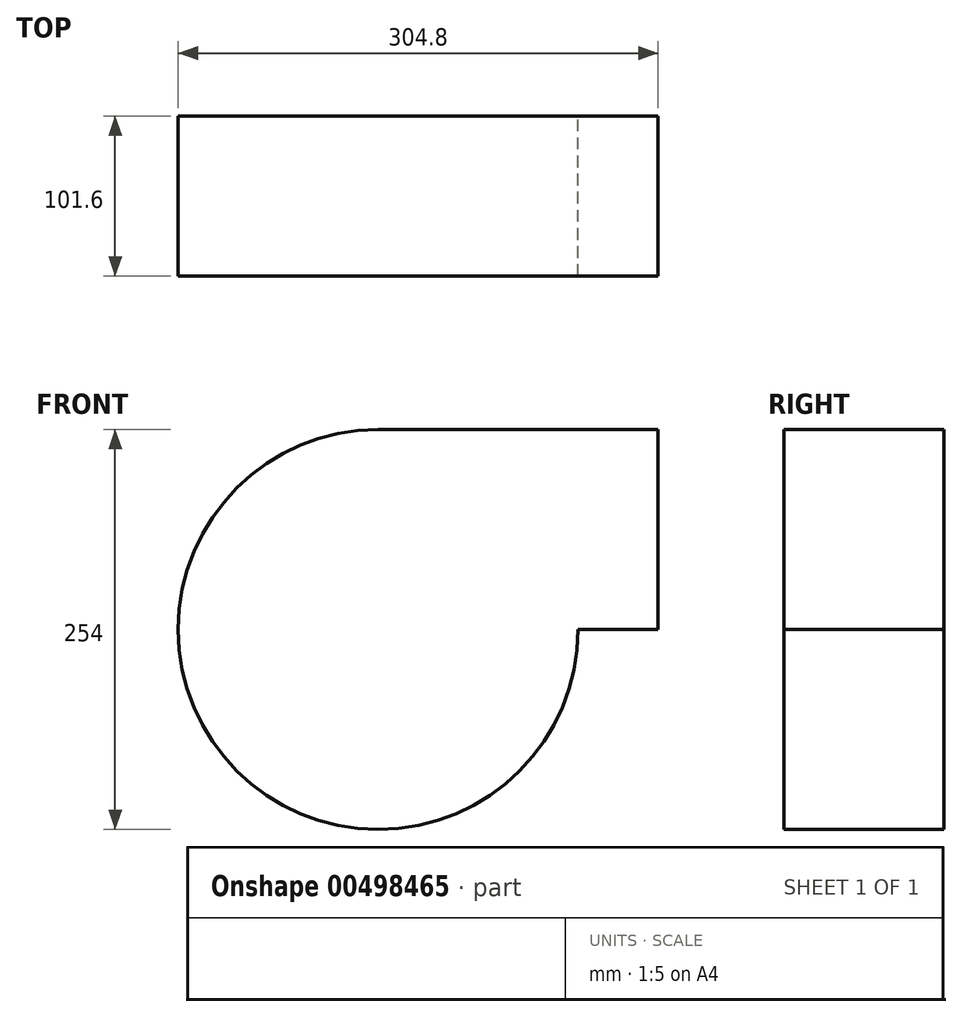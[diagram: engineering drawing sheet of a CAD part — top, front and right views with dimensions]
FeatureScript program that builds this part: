
annotation { "Feature Type Name" : "Feature", "Feature Type Description" : "" }
export const myFeature = defineFeature(function(context is Context, id is Id, definition is map)
    precondition{}
    {
        {
            var Q0;
            Q0=qCreatedBy(makeId("Front.planeOp"),FACE);
            var sketch = newSketch(context, id + "F0", { "sketchPlane" : qUnion([Q0])});
            skCircle(sketch, "E0", {"center": v(0, 0) * mm, "radius": 127 * mm});
            skLineSegment(sketch, "E1.bottom", {"start": v(0, 127) * mm, "end": v(177.8, 127) * mm});
            skLineSegment(sketch, "E1.top", {"start": v(0, 0) * mm, "end": v(177.8, 0) * mm});
            skLineSegment(sketch, "E1.left", {"start": v(0, 127) * mm, "end": v(0, 0) * mm});
            skLineSegment(sketch, "E1.right", {"start": v(177.8, 127) * mm, "end": v(177.8, 0) * mm});
            skSolve(sketch);
        }
        {
            var Q0;
            Q0 = qSketchRegion(id + "F0", true);
            extrude(context, id + "F1", {"entities" : qUnion([Q0]), "depth" : 101.6 * mm});
        }
    });
